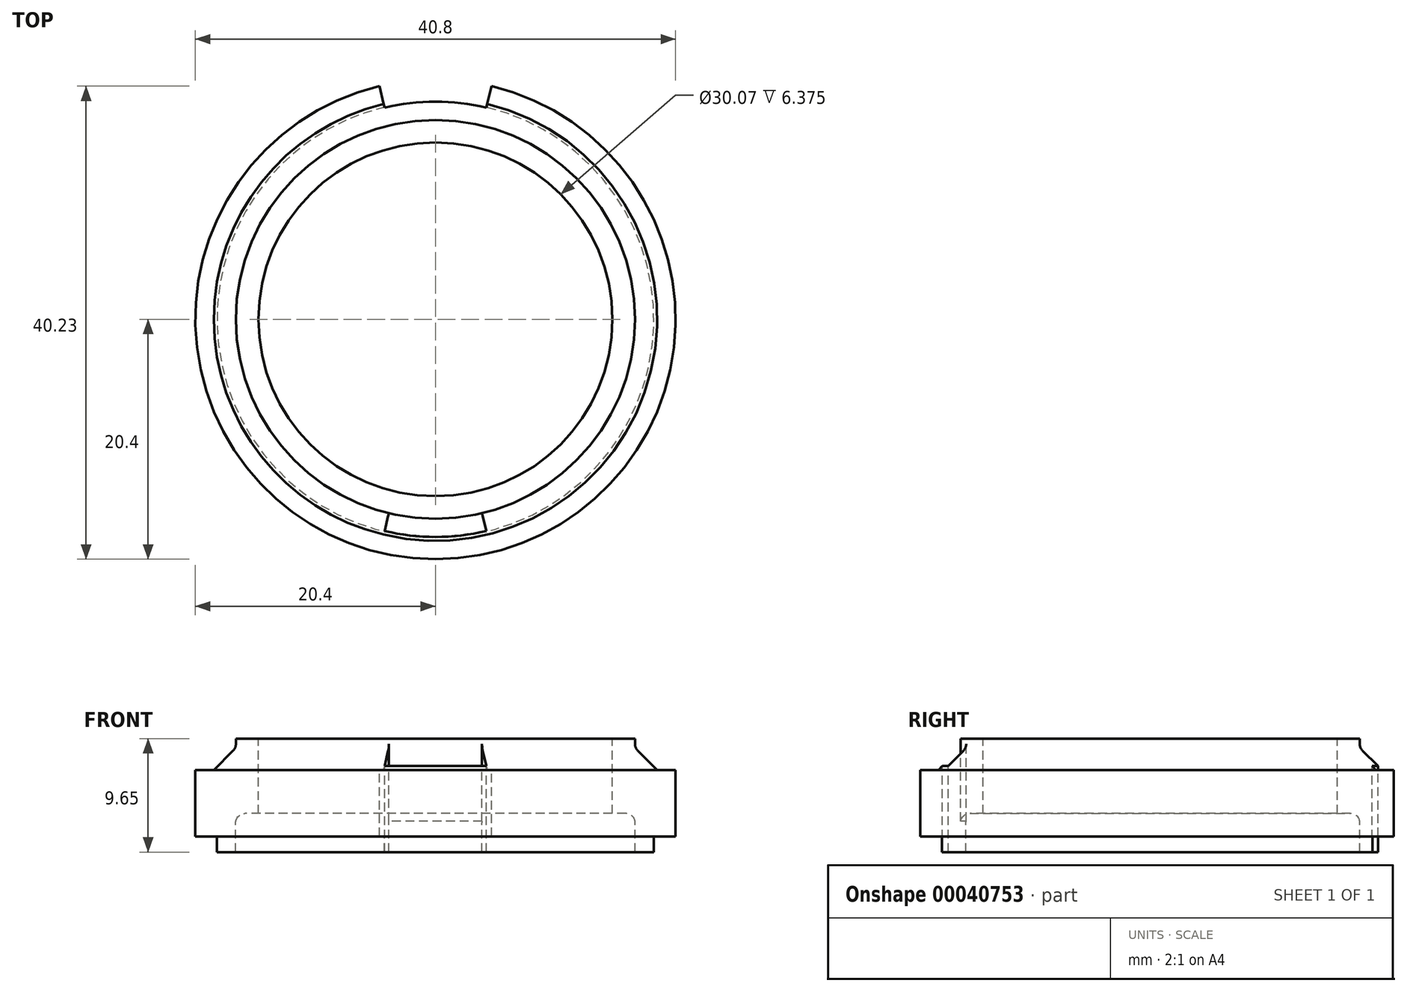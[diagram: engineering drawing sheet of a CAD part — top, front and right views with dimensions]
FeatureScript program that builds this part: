
annotation { "Feature Type Name" : "Feature", "Feature Type Description" : "" }
export const myFeature = defineFeature(function(context is Context, id is Id, definition is map)
    precondition{}
    {
        {
            var Q0;
            Q0=qCreatedBy(makeId("Front.planeOp"),FACE);
            var sketch = newSketch(context, id + "F0", { "sketchPlane" : qUnion([Q0])});
            skLineSegment(sketch, "E0", {"start": v(0, 9.08) * mm, "end": v(0, 0) * mm, "construction": true});
            skLineSegment(sketch, "E1", {"start": v(15.04, 9.65) * mm, "end": v(15.04, 3.28) * mm});
            skLineSegment(sketch, "E2", {"start": v(15.04, 3.28) * mm, "end": v(16.97, 3.28) * mm});
            skLineSegment(sketch, "E3", {"start": v(16.97, 3.28) * mm, "end": v(16.97, 0) * mm});
            skLineSegment(sketch, "E4", {"start": v(16.97, 0) * mm, "end": v(18.55, 0) * mm});
            skLineSegment(sketch, "E5", {"start": v(18.55, 0) * mm, "end": v(18.55, 1.32) * mm});
            skLineSegment(sketch, "E6", {"start": v(18.55, 1.32) * mm, "end": v(20.4, 1.32) * mm});
            skLineSegment(sketch, "E7", {"start": v(20.4, 1.32) * mm, "end": v(20.4, 6.99) * mm});
            skLineSegment(sketch, "E8", {"start": v(20.4, 6.99) * mm, "end": v(18.83, 6.99) * mm});
            skLineSegment(sketch, "E9", {"start": v(18.83, 6.99) * mm, "end": v(16.95, 8.86) * mm});
            skLineSegment(sketch, "E10", {"start": v(16.95, 8.86) * mm, "end": v(16.95, 9.65) * mm});
            skLineSegment(sketch, "E11", {"start": v(16.95, 9.65) * mm, "end": v(15.04, 9.65) * mm});
            skSolve(sketch);
        }
        {
            var Q0;
            Q0=makeQuery(id+"F0.imprint","IMPRINT",FACE,{"disambiguationData":[TD([[makeQuery(id+"F0.imprint","IMPRINT",EDGE,{"derivedFrom":sQuery(id+"F0.wireOp",EDGE,"E1")}),1.0]])]});
            var Q1;
            Q1=sQuery(id+"F0.wireOp",EDGE,"E0");
            revolve(context, id + "F1", {"entities" : qUnion([Q0]), "axis" : qUnion([Q1]), "revolveType" : RevolveType.FULL});
        }
        {
            var Q0;
            Q0=makeQuery(id+"F1.opRevolve","SWEPT_EDGE",EDGE,{"disambiguationData":[OSD([sQuery(id+"F0.wireOp",EDGE,"E2"),sQuery(id+"F0.wireOp",EDGE,"E3")])]});
            fillet(context, id + "F2", {"entities" : qUnion([Q0]), "radius" : 0.8 * mm, "tangentPropagation" : true, "allowEdgeOverflow" : false});
        }
        {
            var Q0;
            Q0=makeQuery(id+"F1.opRevolve","SWEPT_FACE",FACE,{"disambiguationData":[OSD([sQuery(id+"F0.wireOp",EDGE,"E11")])]});
            var sketch = newSketch(context, id + "F3", { "sketchPlane" : qUnion([Q0])});
            skLineSegment(sketch, "E12", {"start": v(0, 0) * mm, "end": v(-4.76, 19.83) * mm});
            skLineSegment(sketch, "E13", {"start": v(4.76, 19.83) * mm, "end": v(0, 0) * mm});
            skArc(sketch, "E14.0", {"start": v(4.76, 19.83) * mm, "mid": v(0, 20.4) * mm, "end": v(-4.76, 19.83) * mm});
            skArc(sketch, "E15", {"start": v(4.32, 18) * mm, "mid": v(0, 18.5) * mm, "end": v(-4.32, 18) * mm});
            skPoint(sketch, "E16", {"position": v(0, 20.4) * mm});
            skLineSegment(sketch, "E17.MirrorCS", {"start": v(0, 0) * mm, "end": v(-4.76, -19.83) * mm});
            skArc(sketch, "E18.MirrorCS", {"start": v(4.32, -18) * mm, "mid": v(0, -18.5) * mm, "end": v(-4.32, -18) * mm});
            skArc(sketch, "E19.MirrorCS", {"start": v(4.76, -19.83) * mm, "mid": v(0, -20.4) * mm, "end": v(-4.76, -19.83) * mm});
            skPoint(sketch, "E20.MirrorP", {"position": v(0, -20.4) * mm});
            skLineSegment(sketch, "E21.MirrorCS", {"start": v(4.76, -19.83) * mm, "end": v(0, 0) * mm});
            skSolve(sketch);
        }
        {
            var Q0;
            {var subQ0=sQuery(id+"F3.wireOp",EDGE,"E14.0");Q0=makeQuery(id+"F3.imprint","IMPRINT",FACE,{"disambiguationData":[TD([[makeQuery(id+"F3.imprint","IMPRINT",EDGE,{"derivedFrom":subQ0}),1.0]])]});}
            var Q1;
            {var subQ2=sQuery(id+"F3.wireOp",EDGE,"E18.MirrorCS");Q1=makeQuery(id+"F3.imprint","IMPRINT",FACE,{"disambiguationData":[TD([[makeQuery(id+"F3.imprint","IMPRINT",EDGE,{"derivedFrom":subQ2}),1.0]])]});}
            extrude(context, id + "F4", {"entities" : qUnion([Q0, Q1]), "operationType" : NewBodyOperationType.REMOVE, "endBound" : BoundingType.THROUGH_ALL, "oppositeDirection" : true, "depth" : 25.4 * mm});
        }
        {
            var Q0;
            Q0=makeQuery(id+"F1.opRevolve","SWEPT_EDGE",EDGE,{"disambiguationData":[OSD([sQuery(id+"F0.wireOp",EDGE,"E9"),sQuery(id+"F0.wireOp",EDGE,"E10")])]});
            fillet(context, id + "F5", {"entities" : qUnion([Q0]), "radius" : 0.8 * mm, "tangentPropagation" : true, "allowEdgeOverflow" : false});
        }
    });
